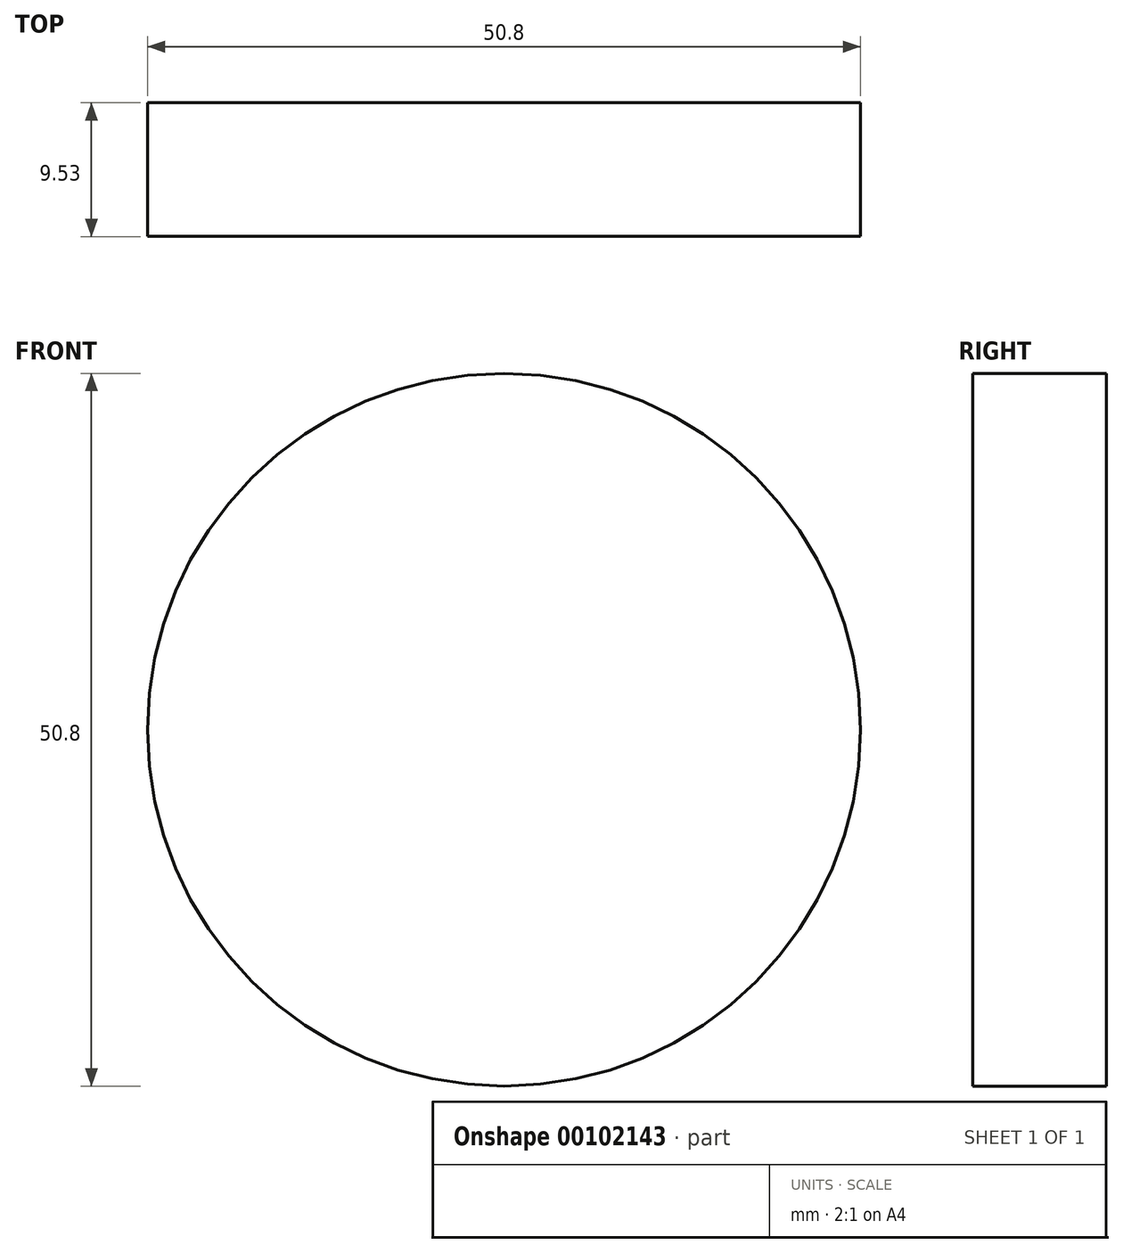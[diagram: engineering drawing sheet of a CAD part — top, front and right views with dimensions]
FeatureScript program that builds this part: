
annotation { "Feature Type Name" : "Feature", "Feature Type Description" : "" }
export const myFeature = defineFeature(function(context is Context, id is Id, definition is map)
    precondition{}
    {
        {
            var Q0;
            Q0=qCreatedBy(makeId("Front.planeOp"),FACE);
            var sketch = newSketch(context, id + "F0", { "sketchPlane" : qUnion([Q0])});
            skCircle(sketch, "E0", {"center": v(0, 0) * mm, "radius": 25.4 * mm});
            skSolve(sketch);
        }
        {
            var Q0;
            Q0 = qSketchRegion(id + "F0", true);
            extrude(context, id + "F1", {"entities" : qUnion([Q0]), "depth" : 9.52 * mm});
        }
    });
